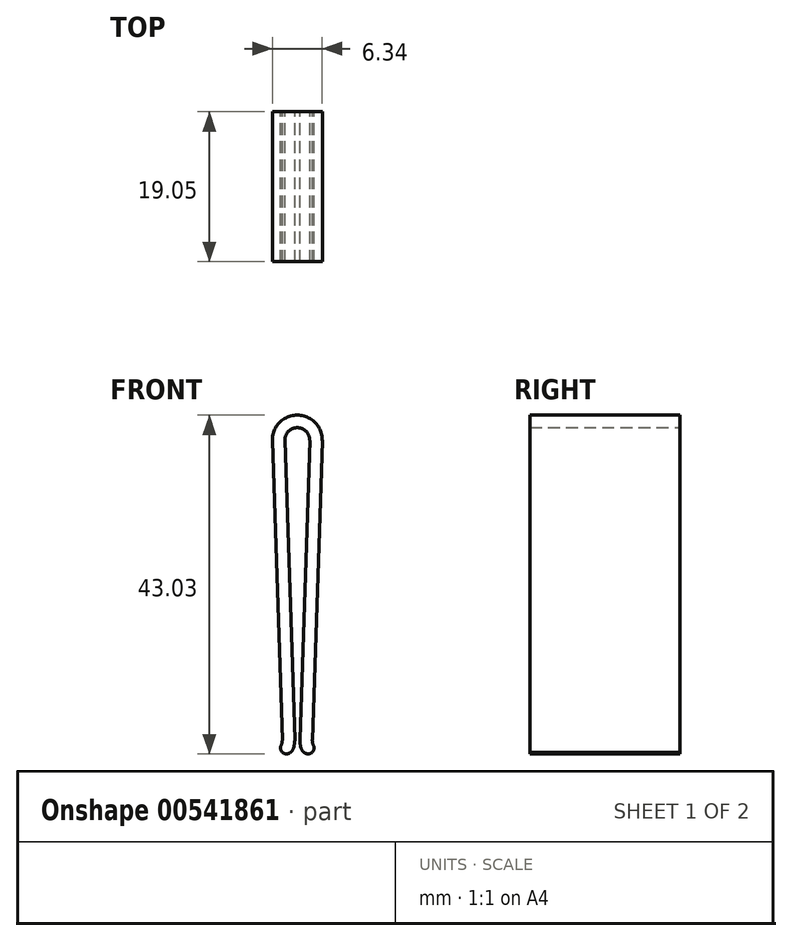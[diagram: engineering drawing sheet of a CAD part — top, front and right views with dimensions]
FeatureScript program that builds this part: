
annotation { "Feature Type Name" : "Feature", "Feature Type Description" : "" }
export const myFeature = defineFeature(function(context is Context, id is Id, definition is map)
    precondition{}
    {
        {
            var Q0;
            Q0=qCreatedBy(makeId("Front.planeOp"),FACE);
            var sketch = newSketch(context, id + "F0", { "sketchPlane" : qUnion([Q0])});
            skCircle(sketch, "E0", {"center": v(0, 0) * mm, "radius": 1.59 * mm});
            skCircle(sketch, "E1", {"center": v(0, 0) * mm, "radius": 3.18 * mm});
            skCircle(sketch, "E2", {"center": v(-3.5, -38.1) * mm, "radius": 1.59 * mm});
            skCircle(sketch, "E3", {"center": v(-3.5, -38.1) * mm, "radius": 3.18 * mm});
            skLineSegment(sketch, "E4", {"start": v(0, 0) * mm, "end": v(0, -49.03) * mm, "construction": true});
            skCircle(sketch, "E5.MirrorC", {"center": v(3.5, -38.1) * mm, "radius": 3.18 * mm});
            skCircle(sketch, "E6.MirrorC", {"center": v(3.5, -38.1) * mm, "radius": 1.59 * mm});
            skLineSegment(sketch, "E7", {"start": v(-1.59, -0.05) * mm, "end": v(-0.32, -38) * mm});
            skLineSegment(sketch, "E8", {"start": v(-3.17, -0.1) * mm, "end": v(-1.9, -38.05) * mm});
            skLineSegment(sketch, "E9.MirrorCS", {"start": v(1.59, -0.05) * mm, "end": v(0.32, -38) * mm});
            skLineSegment(sketch, "E10.MirrorCS", {"start": v(3.17, -0.1) * mm, "end": v(1.9, -38.05) * mm});
            skLineSegment(sketch, "E11", {"start": v(-2.37, -39.22) * mm, "end": v(-1.25, -40.35) * mm});
            skLineSegment(sketch, "E12", {"start": v(-3.5, -38.1) * mm, "end": v(-3.5, -41.27) * mm, "construction": true});
            skLineSegment(sketch, "E13.MirrorCS", {"start": v(2.37, -39.22) * mm, "end": v(1.25, -40.35) * mm});
            skSolve(sketch);
        }
        {
            var Q0;
            {var subQ3=sQuery(id+"F0.wireOp",EDGE,"E7");var subQ4=sQuery(id+"F0.wireOp",EDGE,"E0");var subQ5=makeQuery(id+"F0.imprint","INTERSECT",VERTEX,{"derivedFrom":[subQ4,subQ3]});Q0=makeQuery(id+"F0.imprint","IMPRINT",FACE,{"disambiguationData":[TD([[makeQuery(id+"F0.imprint","IMPRINT",EDGE,{"disambiguationData":[TD([[subQ5,1.0]])],"derivedFrom":subQ4}),-1.0]])]});}
            var Q1;
            {var subQ0=sQuery(id+"F0.wireOp",EDGE,"E8");var subQ1=sQuery(id+"F0.wireOp",EDGE,"E1");var subQ2=makeQuery(id+"F0.imprint","INTERSECT",VERTEX,{"derivedFrom":[subQ1,subQ0]});Q1=makeQuery(id+"F0.imprint","IMPRINT",FACE,{"disambiguationData":[TD([[makeQuery(id+"F0.imprint","IMPRINT",EDGE,{"disambiguationData":[TD([[subQ2,-1.0]])],"derivedFrom":subQ1}),-1.0]])]});}
            var Q2;
            {var subQ0=sQuery(id+"F0.wireOp",EDGE,"E10.MirrorCS");var subQ1=sQuery(id+"F0.wireOp",EDGE,"E1");var subQ2=makeQuery(id+"F0.imprint","INTERSECT",VERTEX,{"derivedFrom":[subQ1,subQ0]});Q2=makeQuery(id+"F0.imprint","IMPRINT",FACE,{"disambiguationData":[TD([[makeQuery(id+"F0.imprint","IMPRINT",EDGE,{"disambiguationData":[TD([[subQ2,1.0]])],"derivedFrom":subQ1}),-1.0]])]});}
            var Q3;
            {var subQ6=sQuery(id+"F0.wireOp",EDGE,"E11");Q3=makeQuery(id+"F0.imprint","IMPRINT",FACE,{"disambiguationData":[TD([[makeQuery(id+"F0.imprint","IMPRINT",EDGE,{"derivedFrom":subQ6}),1.0]])]});}
            var Q4;
            {var subQ3=sQuery(id+"F0.wireOp",EDGE,"E13.MirrorCS");Q4=makeQuery(id+"F0.imprint","IMPRINT",FACE,{"disambiguationData":[TD([[makeQuery(id+"F0.imprint","IMPRINT",EDGE,{"derivedFrom":subQ3}),-1.0]])]});}
            extrude(context, id + "F1", {"entities" : qUnion([Q0, Q1, Q2, Q3, Q4]), "depth" : 19.05 * mm, "offsetDistance" : 25.4 * mm});
        }
        {
            var Q0;
            Q0=makeQuery(id+"F1.opExtrude","SWEPT_EDGE",EDGE,{"disambiguationData":[OSD([sQuery(id+"F0.wireOp",EDGE,"E2"),sQuery(id+"F0.wireOp",EDGE,"E11")])]});
            var Q1;
            Q1=makeQuery(id+"F1.opExtrude","SWEPT_EDGE",EDGE,{"disambiguationData":[OSD([sQuery(id+"F0.wireOp",EDGE,"E3"),sQuery(id+"F0.wireOp",EDGE,"E11")])]});
            var Q2;
            Q2=makeQuery(id+"F1.opExtrude","SWEPT_EDGE",EDGE,{"disambiguationData":[OSD([sQuery(id+"F0.wireOp",EDGE,"E5.MirrorC"),sQuery(id+"F0.wireOp",EDGE,"E13.MirrorCS")])]});
            var Q3;
            Q3=makeQuery(id+"F1.opExtrude","SWEPT_EDGE",EDGE,{"disambiguationData":[OSD([sQuery(id+"F0.wireOp",EDGE,"E6.MirrorC"),sQuery(id+"F0.wireOp",EDGE,"E13.MirrorCS")])]});
            fillet(context, id + "F2", {"entities" : qUnion([Q0, Q1, Q2, Q3]), "radius" : 0.89 * mm, "tangentPropagation" : true, "allowEdgeOverflow" : false});
        }
    });
